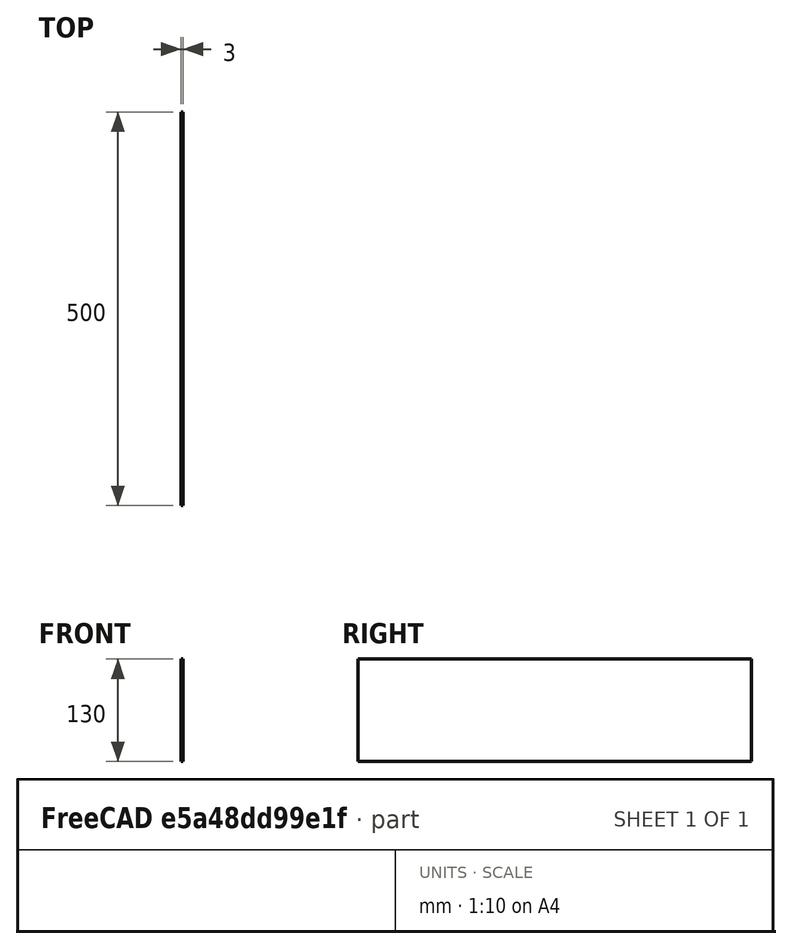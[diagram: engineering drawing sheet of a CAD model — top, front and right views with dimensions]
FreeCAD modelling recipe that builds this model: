
FCSTD DOCUMENT  (FreeCAD 0.18R16131 (Git))
Label: 7000_Marquee_window
License: All rights reserved
LicenseURL: http://en.wikipedia.org/wiki/All_rights_reserved
objects: Sketcher::SketchObject×1, Spreadsheet::Sheet×1, PartDesign::Pad×1, PartDesign::Body×1
note: 4 computed .brp shape members not serialized (recipe doc carries the construction recipe); baked Part::Feature solids carry a one-line shape summary decoded from their .brp

FEATURE [Sketcher::SketchObject] Sketch
  MapMode = 4
  Placement = pos=(0,0,0) rot=(0.57735,0.57735,0.57735;2.0944rad)
  Support = -> [XY_Plane]
  expr: Constraints[6] = Spreadsheet.nY
  expr: Constraints[5] = Spreadsheet.nZ
  sketch-geometry (5):
    g0: LineSegment StartX=0 StartY=0 StartZ=0 EndX=0 EndY=130 EndZ=0
    g1: LineSegment StartX=500 StartY=0 StartZ=0 EndX=500 EndY=130 EndZ=0
    g2: LineSegment StartX=500 StartY=130 StartZ=0 EndX=0 EndY=130 EndZ=0
    g3: LineSegment StartX=250 StartY=0 StartZ=0 EndX=0 EndY=0 EndZ=0
    g4: LineSegment StartX=500 StartY=0 StartZ=0 EndX=250 EndY=0 EndZ=0
  constraints (14):
    c: Vertical(g0)
    c: Vertical(g1)
    c: Coincident(g2,g1)
    c: Coincident(g2,g0)
    c: Horizontal(g2)
    c: DistanceY(g1,g1) = 130
    c: DistanceX(g2,g2) = 500
    c: Coincident(g3,g0)
    c: Coincident(g4,g1)
    c: Horizontal(g4)
    c: Equal(g3,g4)
    c: Coincident(g4,g3)
    c: Horizontal(g3)
    c: Coincident(g0,g-1)
FEATURE [Spreadsheet::Sheet] Spreadsheet  label="xls"
  cells = B7=Marquee Window; B8=Width; C8=nY; D8(nY)=500; B9=Height; C9=nZ; D9(nZ)=130; E9=F(T); B10=Thickness; C10=nT; D10(nT)=3
FEATURE [PartDesign::Pad] Pad
  Length = 3
  Length2 = 100
  Profile = -> Sketch
  Reversed = true
  Type = 0
  expr: Length = Spreadsheet.nT
FEATURE [PartDesign::Body] Body
  Group = -> [Sketch,Pad]
  Origin = -> Origin
  Placement = pos=(428,0,50) rot=(0,0,1;0rad)
  Tip = -> Pad
